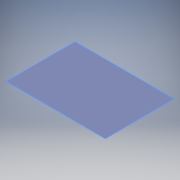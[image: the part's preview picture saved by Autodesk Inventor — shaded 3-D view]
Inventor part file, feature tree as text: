
AUTODESK INVENTOR PART (.ipt)
format: ipt  version: 2018 (Build 220112000, 112)  size: 90,624 bytes
history: native  units: mm
features: reference x4, other x3, extrude x1, sketch x1
ambient origin geometry x8: Origin, YZ Plane, XZ Plane, XY Plane, X Axis, Y Axis, Z Axis, Center Point
bodies: Volumenkörper1 (feature_tree)
feature tree (9):
  extrude  "Extrusion1"  [1 undecoded]
  sketch  "Skizze1"  dims[d0=0.01mm d1=0.0mm]
  reference  "Referenz1"
  reference  "Referenz2"
  reference  "Referenz3"
  reference  "Referenz4"
  parser-record x1  (decoder bookkeeping rows leaked as tree rows — omitted from the tree; the rows remain in map.json)
  other  "Montiert.iam"
  other  "Gegenhalter:1"
note: 1 required parameter value undecoded (feature->parameter linkage not recoverable at this tier; creation-order binding heuristic only, values carry confidence <= 0.55)
note: 1 file-system path scrubbed to <path> (originals preserved in map.json)
